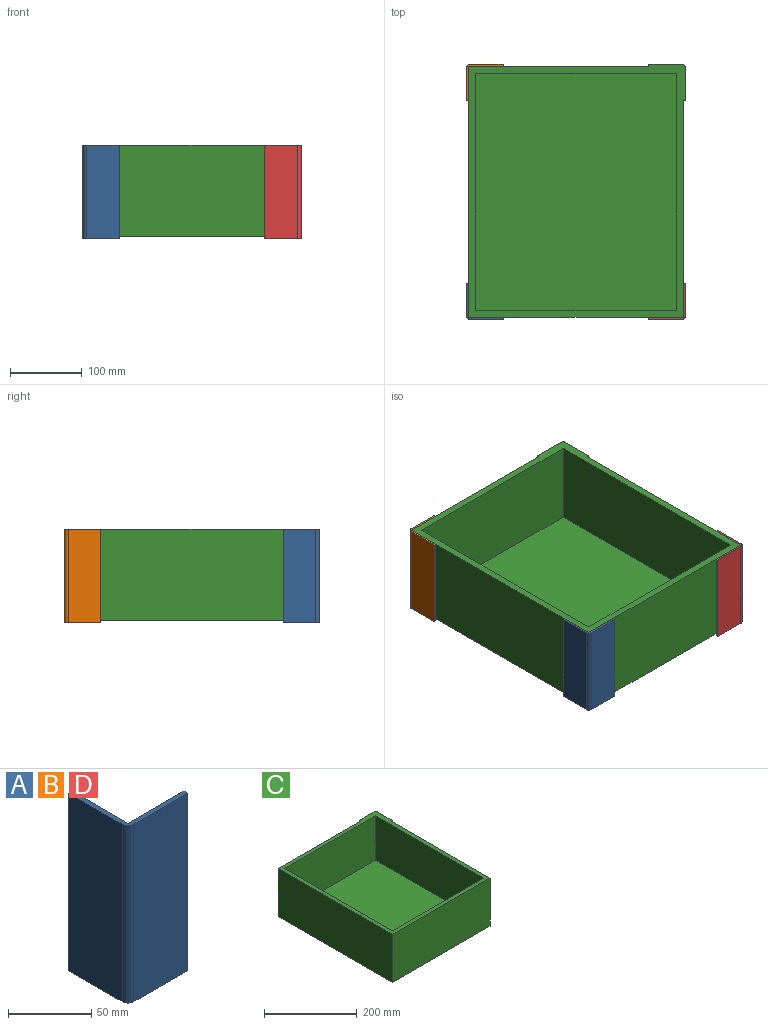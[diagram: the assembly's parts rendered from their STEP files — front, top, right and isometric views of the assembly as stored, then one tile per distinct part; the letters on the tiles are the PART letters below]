
ASSEMBLY  parts=4 mates=9
PART A: 12 faces, bbox 50.8x50.8x130.8 mm
  f0: plane 130.81x3.18mm, normal (0,1,0), area 415.3mm2, adj f1,f5,f6,f7,f9
  f1: plane 130.81x45.72mm, normal (-1,0,0), area 5980.6mm2, adj f0,f6,f9,f11
  f2: plane 130.81x45.72mm, normal (0,-1,0), area 5980.6mm2, adj f3,f6,f9,f11
  f3: plane 130.81x3.18mm, normal (1,0,0), area 415.3mm2, adj f2,f4,f6,f7,f9
  f4: plane 127x47.63mm, normal (0,1,0), area 6048.4mm2, adj f3,f5,f6,f10
  f5: plane 127x47.63mm, normal (1,0,0), area 6048.4mm2, adj f0,f4,f6,f10
  f6: plane 50.8x50.8mm, normal (0,0,1), area 307mm2, adj f0,f1,f2,f3,f4,f5,f11
  f7: plane 47.63x47.63mm, normal (0.71,0.71,0), area 256.6mm2, adj f0,f3,f9,f10
  f8: cylinder r=1.59mm len=3.81mm, axis (0,0,1), area 38mm2, adj f9,f10
  f9: plane 50.8x50.8mm, normal (0,0,-1), area 1433.1mm2, adj f0,f1,f2,f3,f7,f8,f11
  f10: plane 47.63x47.63mm, normal (0,0,1), area 1126.2mm2, adj f4,f5,f7,f8
  f11: cylinder r=5.08mm len=130.81mm, axis (0,0,1), area 1043.8mm2, adj f1,f2,f6,f9
PART B: same geometry as A
PART C: 16 faces, bbox 301.6x352.4x127 mm
  f0: plane 352.43x301.63mm, normal (0,0,-1), area 104540.6mm2, adj f5,f6,f7,f8,f11,f12,f13,f14
  f1: plane 330.2x117.48mm, normal (-1,0,0), area 38790.2mm2, adj f2,f4,f9,f10
  f2: plane 279.4x117.48mm, normal (0,-1,0), area 32822.5mm2, adj f1,f3,f9,f10
  f3: plane 330.2x117.48mm, normal (1,0,0), area 38790.2mm2, adj f2,f4,f9,f10
  f4: plane 279.4x117.48mm, normal (0,1,0), area 32822.5mm2, adj f1,f3,f9,f10
  f5: plane 301.63x127mm, normal (1,0,0), area 38306.4mm2, adj f0,f6,f9,f11
  f6: plane 298.45x127mm, normal (0,-1,0), area 37903.1mm2, adj f0,f5,f7,f9
  f7: plane 349.25x127mm, normal (-1,0,0), area 44354.7mm2, adj f0,f6,f8,f9
  f8: plane 250.83x127mm, normal (0,1,0), area 31854.8mm2, adj f0,f7,f9,f14
  f9: plane 352.43x301.63mm, normal (0,0,1), area 12282.7mm2, adj f1,f2,f3,f4,f5,f6,f7,f8
  f10: plane 330.2x279.4mm, normal (0,0,1), area 92257.9mm2, adj f1,f2,f3,f4
  f11: plane 127x3.18mm, normal (0,-1,0), area 403.2mm2, adj f0,f5,f9,f12
  f12: plane 127x45.72mm, normal (1,0,0), area 5806.4mm2, adj f0,f9,f11,f15
  f13: plane 127x45.72mm, normal (0,1,0), area 5806.4mm2, adj f0,f9,f14,f15
  f14: plane 127x3.18mm, normal (-1,0,0), area 403.2mm2, adj f0,f8,f9,f13
  f15: cylinder r=5.08mm len=127mm, axis (0,0,1), area 1013.4mm2, adj f0,f9,f12,f13
PART D: same geometry as A
PLACE A t=(-152.4,-177.8,0)mm
PLACE B rot(axis=(0,0,-1),90deg) t=(-152.4,177.8,0)mm
PLACE C at identity fixed
PLACE D rot(axis=(0,0,1),90deg) t=(152.4,-177.8,0)mm
MATE planar B.f5 <-> C.f8  axis (0,-1,0) through (-125.41,174.63,63.5)mm
MATE planar D.f5 <-> A.f4  axis (0,1,0) through (125.41,-174.63,63.5)mm
MATE planar C.f0 <-> A.f10  axis (0,0,-1) through (0.41,0.48,0)mm
MATE planar D.f4 <-> C.f5  axis (-1,0,0) through (149.23,-150.81,63.5)mm
MATE planar D.f10 <-> C.f0  axis (0,0,1) through (133.32,-158.72,0)mm
MATE planar C.f0 <-> B.f10  axis (0,0,-1) through (0.41,0.48,0)mm
MATE planar B.f4 <-> C.f7  axis (1,0,0) through (-149.23,150.81,63.5)mm
MATE planar C.f7 <-> A.f5  axis (-1,0,0) through (-149.23,0,63.5)mm
MATE planar C.f6 <-> A.f4  axis (0,-1,0) through (0,-174.63,63.5)mm
